# Revit family: 84121_HOST_FACE
name_source: partatom
category: Lighting Fixtures
revit_build: Autodesk Revit MEP 2015 (Build: 20140323_1530(x64)
units: mm (PartAtom-declared; Revit-internal decimal feet)

## types (4) — shared parameters
Color Filter = 16777215
Dimming Lamp Color Temperature Shift = <None>
Manufacturer = BEGA-US
Telephone = 805.684.0533
Tilt Angle = 90.00°
URL = www.bega-us.com

## per-type parameters (varying)
| type | Default Elevation | Description | Lamp | Model | Photometric Web File |
| Wall Luminaires - Directed Light | 6' - 0" | Surface wall with cutoff optics | 44.6W LED | 2260LED | generic |
| Wall Luminaires - Linear | 6' - 0" | Suface wall - linear with white acrylic diffuser | (1) 39W CF twin-4-p | 4425P | generic |
| Ceiling and Wall Luminaires - Unshielded | 0' - 0" |  | 32.0W LED | 84 120 | 84120.ies |
| Pole-top luminaires with symmetrical light distribution | 0' - 0" | LED pole-top luminaire - asymmetric | 32.0W LED | 84 121 | 84121.ies |

## geometry (parser evidence)
native form markers: Blend x18, Sweep x16
no freeform markers — native parametric forms only
